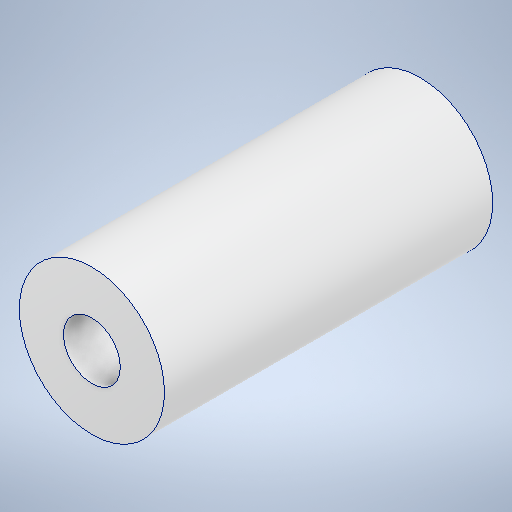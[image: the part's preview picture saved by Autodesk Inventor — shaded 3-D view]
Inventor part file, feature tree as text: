
AUTODESK INVENTOR PART (.ipt)
format: ipt  version: 2025.1 (Build 291241020, 241B)  size: 226,816 bytes
history: native  units: in
note: dims shown in document units (in); Inventor stores cm internally (conversion verified against a paired STEP export)
features: extrude x1, sketch x1
ambient origin geometry x8: Origin, YZ Plane, XZ Plane, XY Plane, X Axis, Y Axis, Z Axis, Center Point
bodies: Solid1 (feature_tree)
feature tree (2):
  extrude  "Extrusion1"  Depth=1.131in
  sketch  "Sketch1"  dims[d0=0.196in d1=0.5in d2=1.131in d3=0.0in]
